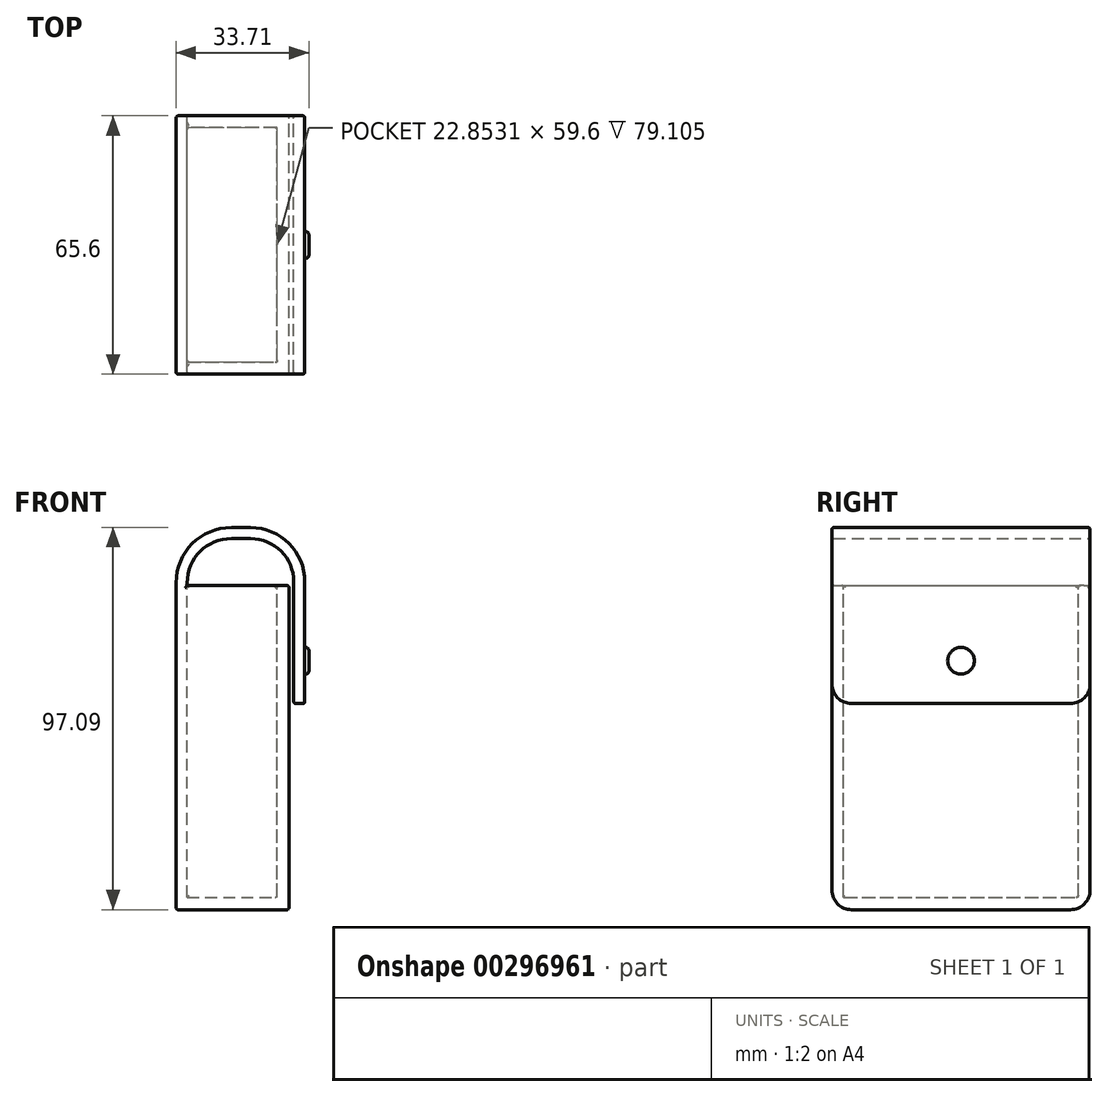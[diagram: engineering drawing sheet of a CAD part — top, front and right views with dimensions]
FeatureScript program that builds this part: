
annotation { "Feature Type Name" : "Feature", "Feature Type Description" : "" }
export const myFeature = defineFeature(function(context is Context, id is Id, definition is map)
    precondition{}
    {
        {
            var Q0;
            Q0=qCreatedBy(makeId("Front.planeOp"),FACE);
            var sketch = newSketch(context, id + "F0", { "sketchPlane" : qUnion([Q0])});
            skLineSegment(sketch, "E0.bottom", {"start": v(-10.32, 19.1) * mm, "end": v(18.34, 19.1) * mm});
            skLineSegment(sketch, "E0.top", {"start": v(-10.32, -63.24) * mm, "end": v(18.34, -63.24) * mm});
            skLineSegment(sketch, "E0.left", {"start": v(-10.32, 19.1) * mm, "end": v(-10.32, -63.24) * mm});
            skLineSegment(sketch, "E0.right", {"start": v(18.34, 19.1) * mm, "end": v(18.34, -63.24) * mm});
            skLineSegment(sketch, "E1", {"start": v(-10.32, 19.1) * mm, "end": v(-10.32, 19.8) * mm});
            skLineSegment(sketch, "E2", {"start": v(3.73, 33.85) * mm, "end": v(8.56, 33.85) * mm});
            skLineSegment(sketch, "E3", {"start": v(22.37, 20.05) * mm, "end": v(22.37, -10.87) * mm});
            skPoint(sketch, "E4.visualSharp", {"position": v(-10.32, 33.85) * mm});
            skArc(sketch, "E4.filletArc", {"start": v(3.73, 33.85) * mm, "mid": v(-6.2, 29.74) * mm, "end": v(-10.32, 19.8) * mm});
            skPoint(sketch, "E5.visualSharp", {"position": v(22.37, 33.85) * mm});
            skArc(sketch, "E5.filletArc", {"start": v(22.37, 20.05) * mm, "mid": v(18.32, 29.81) * mm, "end": v(8.56, 33.85) * mm});
            skLineSegment(sketch, "E6.0", {"start": v(19.57, 20.05) * mm, "end": v(19.57, -10.87) * mm});
            skLineSegment(sketch, "E6.1", {"start": v(-7.52, 19.1) * mm, "end": v(-7.52, 19.8) * mm});
            skArc(sketch, "E6.2", {"start": v(3.73, 31.05) * mm, "mid": v(-4.22, 27.76) * mm, "end": v(-7.52, 19.8) * mm});
            skLineSegment(sketch, "E6.3", {"start": v(3.73, 31.05) * mm, "end": v(8.56, 31.05) * mm});
            skArc(sketch, "E6.4", {"start": v(19.57, 20.05) * mm, "mid": v(16.34, 27.83) * mm, "end": v(8.56, 31.05) * mm});
            skLineSegment(sketch, "E7", {"start": v(19.57, -10.87) * mm, "end": v(22.37, -10.87) * mm});
            skSolve(sketch);
        }
        {
            var Q0;
            {var subQ1=sQuery(id+"F0.wireOp",EDGE,"E1");Q0=makeQuery(id+"F0.imprint","IMPRINT",FACE,{"disambiguationData":[TD([[makeQuery(id+"F0.imprint","IMPRINT",EDGE,{"derivedFrom":subQ1}),-1.0]])]});}
            var Q1;
            Q1=makeQuery(id+"F0.imprint","IMPRINT",FACE,{"disambiguationData":[TD([[makeQuery(id+"F0.imprint","IMPRINT",EDGE,{"derivedFrom":sQuery(id+"F0.wireOp",EDGE,"E0.top")}),1.0]])]});
            extrude(context, id + "F1", {"entities" : qUnion([Q0, Q1]), "depth" : 65.6 * mm, "offsetDistance" : 25 * mm, "symmetric" : true});
        }
        {
            var Q0;
            Q0=makeQuery(id+"F1.opExtrude","SWEPT_FACE",FACE,{"disambiguationData":[OSD([sQuery(id+"F0.wireOp",EDGE,"E0.bottom")])]});
            var sketch = newSketch(context, id + "F2", { "sketchPlane" : qUnion([Q0])});
            skLineSegment(sketch, "E8", {"start": v(-7.52, -29.8) * mm, "end": v(15.34, -29.8) * mm});
            skLineSegment(sketch, "E9", {"start": v(15.34, -29.8) * mm, "end": v(15.34, 29.8) * mm});
            skLineSegment(sketch, "E10", {"start": v(15.34, 29.8) * mm, "end": v(-7.52, 29.8) * mm});
            skSolve(sketch);
        }
        {
            var Q0;
            {var subQ0=sQuery(id+"F2.wireOp",EDGE,"E8");Q0=makeQuery(id+"F2.imprint","IMPRINT",FACE,{"disambiguationData":[TD([[makeQuery(id+"F2.imprint","IMPRINT",EDGE,{"derivedFrom":subQ0}),1.0]])]});}
            extrude(context, id + "F3", {"entities" : qUnion([Q0]), "operationType" : NewBodyOperationType.REMOVE, "oppositeDirection" : true, "depth" : 79.2 * mm, "offsetDistance" : 25 * mm});
        }
        {
            var Q0;
            Q0=makeQuery(id+"F1.opExtrude","CAP_EDGE",EDGE,{"disambiguationData":[OSD([sQuery(id+"F0.wireOp",EDGE,"E7")])],"isStart":false});
            var Q1;
            Q1=makeQuery(id+"F1.opExtrude","CAP_EDGE",EDGE,{"disambiguationData":[OSD([sQuery(id+"F0.wireOp",EDGE,"E7")])],"isStart":true});
            var Q2;
            Q2=makeQuery(id+"F1.opExtrude","CAP_EDGE",EDGE,{"disambiguationData":[OSD([sQuery(id+"F0.wireOp",EDGE,"E0.top")])],"isStart":true});
            var Q3;
            Q3=makeQuery(id+"F1.opExtrude","CAP_EDGE",EDGE,{"disambiguationData":[OSD([sQuery(id+"F0.wireOp",EDGE,"E0.top")])],"isStart":false});
            fillet(context, id + "F4", {"entities" : qUnion([Q0, Q1, Q2, Q3]), "radius" : 5 * mm, "tangentPropagation" : true, "allowEdgeOverflow" : false});
        }
        {
            var Q0;
            Q0=makeQuery(id+"F1.opExtrude","CAP_EDGE",EDGE,{"disambiguationData":[OSD([sQuery(id+"F0.wireOp",EDGE,"E3")])],"isStart":false});
            var Q1;
            Q1=makeQuery(id+"F1.opExtrude","CAP_EDGE",EDGE,{"disambiguationData":[OSD([sQuery(id+"F0.wireOp",EDGE,"E6.3")])],"isStart":false});
            var Q2;
            Q2=makeQuery(id+"F1.opExtrude","CAP_EDGE",EDGE,{"disambiguationData":[OSD([sQuery(id+"F0.wireOp",EDGE,"E0.right")])],"isStart":false});
            var Q3;
            Q3=makeQuery(id+"F1.opExtrude","CAP_EDGE",EDGE,{"disambiguationData":[OSD([sQuery(id+"F0.wireOp",EDGE,"E0.bottom")])],"isStart":false});
            var Q4;
            Q4=makeQuery(id+"F1.opExtrude","SWEPT_EDGE",EDGE,{"disambiguationData":[OSD([sQuery(id+"F0.wireOp",EDGE,"E0.bottom"),sQuery(id+"F0.wireOp",EDGE,"E0.right")])]});
            var Q5;
            Q5=makeQuery(id+"F3.boolean.opBoolean","COPY",EDGE,{"derivedFrom":makeQuery(id+"F3.opExtrude","CAP_EDGE",EDGE,{"disambiguationData":[OSD([sQuery(id+"F2.wireOp",EDGE,"E8")])],"isStart":true})});
            var Q6;
            Q6=makeQuery(id+"F3.boolean.opBoolean","COPY",EDGE,{"derivedFrom":makeQuery(id+"F3.opExtrude","CAP_EDGE",EDGE,{"disambiguationData":[OSD([sQuery(id+"F2.wireOp",EDGE,"E9")])],"isStart":true})});
            var Q7;
            Q7=makeQuery(id+"F3.boolean.opBoolean","COPY",FACE,{"derivedFrom":makeQuery(id+"F3.opExtrude","SWEPT_FACE",FACE,{"disambiguationData":[OSD([sQuery(id+"F2.wireOp",EDGE,"E10")])]})});
            var Q8;
            Q8=makeQuery(id+"F3.boolean.opBoolean","COPY",FACE,{"derivedFrom":makeQuery(id+"F3.opExtrude","SWEPT_FACE",FACE,{"disambiguationData":[OSD([sQuery(id+"F2.wireOp",EDGE,"E9")])]})});
            var Q9;
            Q9=makeQuery(id+"F3.boolean.opBoolean","COPY",FACE,{"derivedFrom":makeQuery(id+"F3.opExtrude","SWEPT_FACE",FACE,{"disambiguationData":[OSD([sQuery(id+"F2.wireOp",EDGE,"E8")])]})});
            fillet(context, id + "F5", {"entities" : qUnion([Q0, Q1, Q2, Q3, Q4, Q5, Q6, Q7, Q8, Q9]), "radius" : 0.5 * mm, "tangentPropagation" : true, "allowEdgeOverflow" : false});
        }
        {
            var Q0;
            Q0=makeQuery(id+"F1.opExtrude","SWEPT_FACE",FACE,{"disambiguationData":[OSD([sQuery(id+"F0.wireOp",EDGE,"E3")])]});
            var sketch = newSketch(context, id + "F6", { "sketchPlane" : qUnion([Q0])});
            skCircle(sketch, "E11", {"center": v(0, 0) * mm, "radius": 3.39 * mm});
            skSolve(sketch);
        }
        {
            var Q0;
            Q0 = qSketchRegion(id + "F6", true);
            extrude(context, id + "F7", {"entities" : qUnion([Q0]), "depth" : 1.02 * mm, "offsetDistance" : 25 * mm});
        }
        {
            var Q0;
            Q0=makeQuery(id+"F7.opExtrude","CAP_FACE",FACE,{"disambiguationData":[OSD([sQuery(id+"F6.wireOp",EDGE,"E11")])],"isStart":false});
            fillet(context, id + "F8", {"entities" : qUnion([Q0]), "radius" : 0.75 * mm, "tangentPropagation" : true, "allowEdgeOverflow" : false});
        }
        {
            var Q0;
            Q0=makeQuery(id+"F7.opExtrude","CAP_EDGE",EDGE,{"disambiguationData":[OSD([sQuery(id+"F6.wireOp",EDGE,"E11")])],"isStart":true});
            fillet(context, id + "F9", {"entities" : qUnion([Q0]), "radius" : 0.1 * mm, "tangentPropagation" : true, "allowEdgeOverflow" : false});
        }
    });
